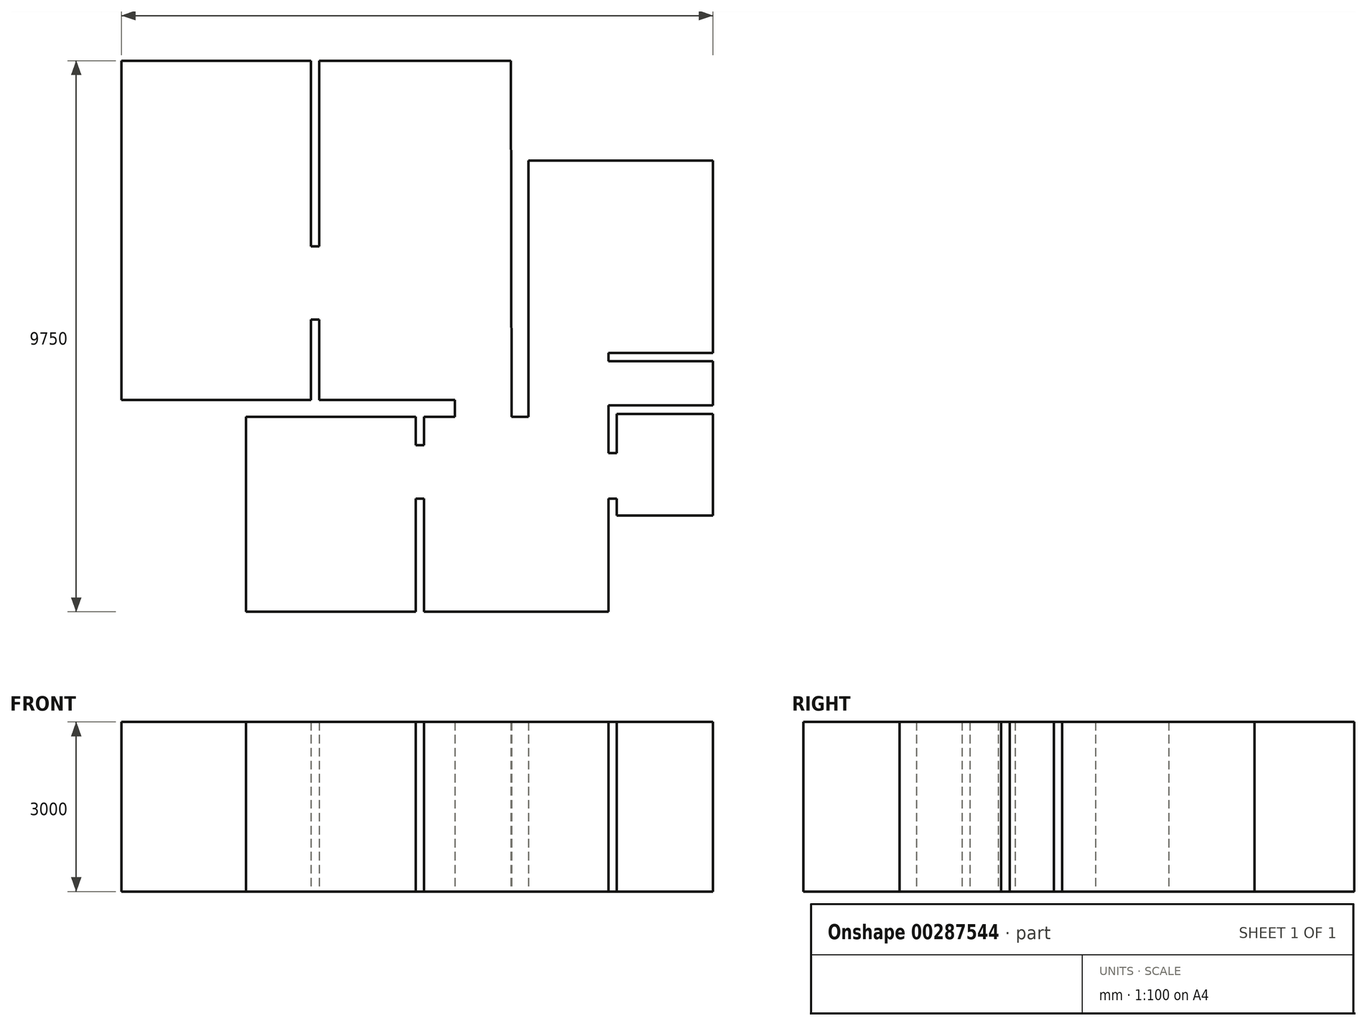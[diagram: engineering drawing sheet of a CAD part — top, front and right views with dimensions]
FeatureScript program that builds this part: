
annotation { "Feature Type Name" : "Feature", "Feature Type Description" : "" }
export const myFeature = defineFeature(function(context is Context, id is Id, definition is map)
    precondition{}
    {
        {
            var Q0;
            Q0=qCreatedBy(makeId("Top.planeOp"),FACE);
            var sketch = newSketch(context, id + "F0", { "sketchPlane" : qUnion([Q0])});
            skLineSegment(sketch, "E0", {"start": v(0, 0) * mm, "end": v(0, -6000) * mm});
            skLineSegment(sketch, "E1", {"start": v(0, -6000) * mm, "end": v(3350, -6000) * mm});
            skLineSegment(sketch, "E2", {"start": v(3350, -6000) * mm, "end": v(3350, -4579.7) * mm});
            skLineSegment(sketch, "E3", {"start": v(3350, -4579.7) * mm, "end": v(3500, -4579.7) * mm});
            skLineSegment(sketch, "E4", {"start": v(3500, -4579.7) * mm, "end": v(3500, -6000) * mm});
            skLineSegment(sketch, "E5", {"start": v(3500, -6000) * mm, "end": v(5900, -6000) * mm});
            skLineSegment(sketch, "E6", {"start": v(5900, -6000) * mm, "end": v(5900, -6300) * mm});
            skLineSegment(sketch, "E7", {"start": v(5900, -6300) * mm, "end": v(5354.38, -6300) * mm});
            skLineSegment(sketch, "E8", {"start": v(5204.38, -6300) * mm, "end": v(2204.38, -6300) * mm});
            skLineSegment(sketch, "E9", {"start": v(2204.38, -6300) * mm, "end": v(2204.38, -9750) * mm});
            skLineSegment(sketch, "E10", {"start": v(2204.38, -9750) * mm, "end": v(5204.38, -9750) * mm});
            skLineSegment(sketch, "E11", {"start": v(5204.38, -9750) * mm, "end": v(5204.38, -7750) * mm});
            skLineSegment(sketch, "E12", {"start": v(5204.38, -7750) * mm, "end": v(5354.38, -7750) * mm});
            skLineSegment(sketch, "E13", {"start": v(5354.38, -7750) * mm, "end": v(5354.38, -9750) * mm});
            skLineSegment(sketch, "E14", {"start": v(5354.38, -9750) * mm, "end": v(8614.38, -9750) * mm});
            skLineSegment(sketch, "E15", {"start": v(8614.38, -9750) * mm, "end": v(8614.38, -7750) * mm});
            skLineSegment(sketch, "E16", {"start": v(8614.38, -7750) * mm, "end": v(8764.38, -7750) * mm});
            skLineSegment(sketch, "E17", {"start": v(8764.38, -7750) * mm, "end": v(8764.38, -8050) * mm});
            skLineSegment(sketch, "E18", {"start": v(8764.38, -8050) * mm, "end": v(10464.38, -8050) * mm});
            skLineSegment(sketch, "E19", {"start": v(10464.38, -8050) * mm, "end": v(10464.38, -6250) * mm});
            skLineSegment(sketch, "E20", {"start": v(10464.38, -6100) * mm, "end": v(8764.38, -6100) * mm});
            skLineSegment(sketch, "E21", {"start": v(10464.38, -6100) * mm, "end": v(10464.38, -5320) * mm});
            skLineSegment(sketch, "E22", {"start": v(10464.38, -5320) * mm, "end": v(8614.38, -5320) * mm});
            skLineSegment(sketch, "E23", {"start": v(8614.38, -5320) * mm, "end": v(8614.38, -5170) * mm});
            skLineSegment(sketch, "E24", {"start": v(8614.38, -5170) * mm, "end": v(10464.38, -5170) * mm});
            skLineSegment(sketch, "E25", {"start": v(10464.38, -5170) * mm, "end": v(10464.38, -1770) * mm});
            skLineSegment(sketch, "E26", {"start": v(6890, 0) * mm, "end": v(3500, 0) * mm});
            skLineSegment(sketch, "E27", {"start": v(3500, 0) * mm, "end": v(3500, -3282.27) * mm});
            skLineSegment(sketch, "E28", {"start": v(3500, -3282.27) * mm, "end": v(3350, -3282.27) * mm});
            skLineSegment(sketch, "E29", {"start": v(3350, -3282.27) * mm, "end": v(3350, 0) * mm});
            skLineSegment(sketch, "E30", {"start": v(3350, 0) * mm, "end": v(0, 0) * mm});
            skLineSegment(sketch, "E31", {"start": v(5204.38, -6300) * mm, "end": v(5204.38, -6800) * mm});
            skLineSegment(sketch, "E32", {"start": v(5204.38, -6800) * mm, "end": v(5354.38, -6800) * mm});
            skLineSegment(sketch, "E33", {"start": v(5354.38, -6800) * mm, "end": v(5354.38, -6300) * mm});
            skLineSegment(sketch, "E34", {"start": v(10464.38, -6250) * mm, "end": v(8764.38, -6250) * mm});
            skLineSegment(sketch, "E35", {"start": v(8764.38, -6100) * mm, "end": v(8614.38, -6100) * mm});
            skLineSegment(sketch, "E36", {"start": v(8614.38, -6100) * mm, "end": v(8614.38, -6945.52) * mm});
            skLineSegment(sketch, "E37", {"start": v(8614.38, -6945.52) * mm, "end": v(8764.38, -6945.52) * mm});
            skLineSegment(sketch, "E38", {"start": v(8764.38, -6945.52) * mm, "end": v(8764.38, -6250) * mm});
            skLineSegment(sketch, "E39", {"start": v(6900, -6300) * mm, "end": v(7200, -6300) * mm});
            skLineSegment(sketch, "E40", {"start": v(7200, -6300) * mm, "end": v(7200, -1770) * mm});
            skLineSegment(sketch, "E41", {"start": v(7200, -1770) * mm, "end": v(10464.38, -1770) * mm});
            skLineSegment(sketch, "E42", {"start": v(6900, -6300) * mm, "end": v(6890, 0) * mm});
            skSolve(sketch);
        }
        {
            var Q0;
            Q0 = qSketchRegion(id + "F0", true);
            extrude(context, id + "F1", {"entities" : qUnion([Q0]), "depth" : 3000 * mm});
        }
    });
